# Revit family: Schutzkappen 45
name_source: partatom
category: HLS-Bauteile
revit_build: Autodesk Revit 2017 (Build: 20190507_1515(x64)
units: mm (PartAtom-declared; Revit-internal decimal feet)

## family parameters
Arbeitsebenenbasiert = Ja
Beim Laden mit Abzugskörper schneiden = Nein
Bemaßung runder Anschluss = Durchmesser verwenden
Gemeinsam genutzt = Ja
Immer vertikal = Nein
Raumberechnungspunkt = Nein
Teiletyp = Normal

## types (4) — shared parameters
B = 45 mm  [stored 0.147638 ft]
C = 37 mm  [stored 0.121391 ft]
Fabrikat = MEFA
Farbe = schwarz
Firma = MEFA Befestigungs- und Montagesysteme GmbH
H1 = 13 mm  [stored 0.0426509 ft]
Kurztext1 = Endkappe C-Profil 45
L1 = 3 mm  [stored 0.00984252 ft]
L2 = 12 mm  [stored 0.0393701 ft]
Material = Kunststoff
Materialname = PE
Mengeneinheit = St
Vorgabe-Ansicht = 1219 mm
vpe = 50 St

## per-type parameters (varying)
| type | Artikelnummer | B1 | B2 | BP | D | EAN | Gewicht | H2 | Kurztext2 | Profiltyp |
| Schutzkappe 45- 26 | 0819005 | 26 mm | 4 mm  [stored 0.0131234 ft] | 4 mm  [stored 0.0131234 ft] | 18 mm  [stored 0.0590551 ft] | 4250928420626 | 0.01 kg | 11 mm  [stored 0.0360892 ft] | für Profil 45/26 PE Schwarz | 45/26 |
| Schutzkappe 45- 45 | 0819036 | 45 mm  [stored 0.147638 ft] | 5 mm  [stored 0.0164042 ft] | 5 mm  [stored 0.0164042 ft] | 36 mm  [stored 0.11811 ft] | 4250928448026 | 0.01 kg | 20 mm  [stored 0.0656168 ft] | für Profil 45/45 PE Schwarz | 45/45 |
| Schutzkappe 45- 60 | 0819042 | 60 mm  [stored 0.19685 ft] | 5 mm  [stored 0.0164042 ft] | 5 mm  [stored 0.0164042 ft] | 52 mm | 4250928420640 | 0.01 kg | 28 mm  [stored 0.0918635 ft] | für Profil 45/60 PE Schwarz | 45/60 |
| Schutzkappe 45- 75 | 0819046 | 75 mm | 5 mm  [stored 0.0164042 ft] | 5 mm  [stored 0.0164042 ft] | 65 mm  [stored 0.213255 ft] | 4250928420657 | 0.02 kg | 36 mm  [stored 0.11811 ft] | für Profil 45/75 PE Schwarz | 45/75 |

note: [stored X ft] marks values corroborated as IEEE doubles in the binary element streams (Revit-internal decimal feet)
